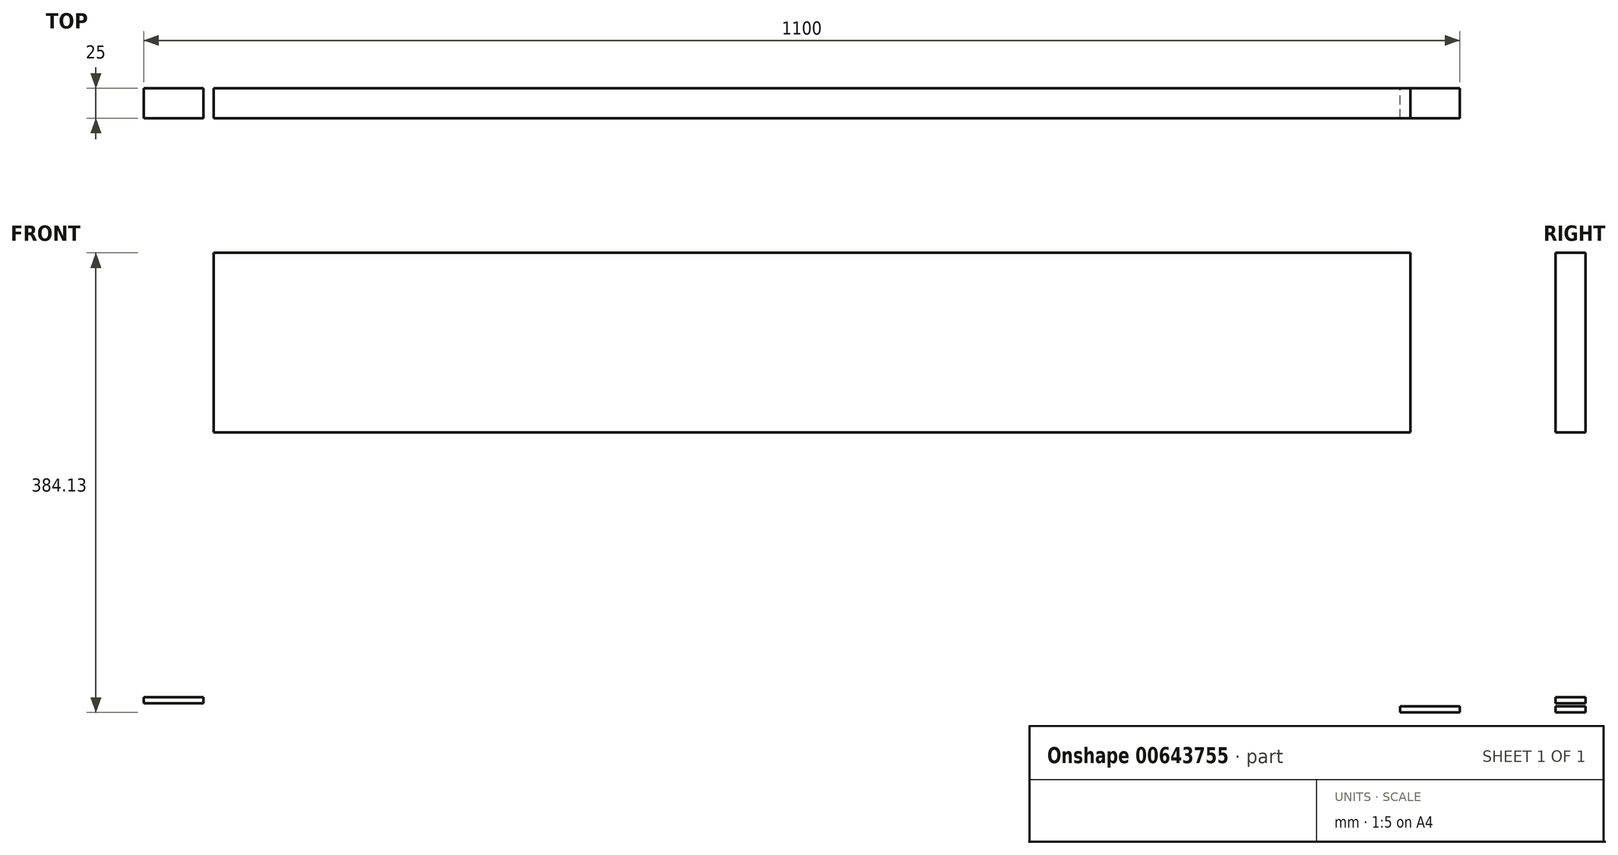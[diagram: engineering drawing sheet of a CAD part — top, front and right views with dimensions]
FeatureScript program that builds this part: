
annotation { "Feature Type Name" : "Feature", "Feature Type Description" : "" }
export const myFeature = defineFeature(function(context is Context, id is Id, definition is map)
    precondition{}
    {
        {
            var Q0;
            Q0=qCreatedBy(makeId("Front.planeOp"),FACE);
            var sketch = newSketch(context, id + "F0", { "sketchPlane" : qUnion([Q0])});
            skLineSegment(sketch, "E0.bottom", {"start": v(-524.12, -83.88) * mm, "end": v(-574.12, -83.88) * mm});
            skLineSegment(sketch, "E0.top", {"start": v(-524.12, -88.88) * mm, "end": v(-574.12, -88.88) * mm});
            skLineSegment(sketch, "E0.left", {"start": v(-524.12, -83.88) * mm, "end": v(-524.12, -88.88) * mm});
            skLineSegment(sketch, "E0.right", {"start": v(-574.12, -83.88) * mm, "end": v(-574.12, -88.88) * mm});
            skLineSegment(sketch, "E1.bottom", {"start": v(525.88, -91.45) * mm, "end": v(475.88, -91.45) * mm});
            skLineSegment(sketch, "E1.top", {"start": v(525.88, -96.45) * mm, "end": v(475.88, -96.45) * mm});
            skLineSegment(sketch, "E1.left", {"start": v(525.88, -91.45) * mm, "end": v(525.88, -96.45) * mm});
            skLineSegment(sketch, "E1.right", {"start": v(475.88, -91.45) * mm, "end": v(475.88, -96.45) * mm});
            skLineSegment(sketch, "E2.bottom", {"start": v(-308.87, 130.07) * mm, "end": v(-358.87, 130.07) * mm});
            skLineSegment(sketch, "E2.left", {"start": v(-308.87, 130.07) * mm, "end": v(-308.87, 125.07) * mm});
            skLineSegment(sketch, "E2.right", {"start": v(-358.87, 130.07) * mm, "end": v(-358.87, 125.07) * mm});
            skSolve(sketch);
        }
        {
            var Q0;
            Q0=makeQuery(id+"F0.imprint","IMPRINT",FACE,{"disambiguationData":[TD([[makeQuery(id+"F0.imprint","IMPRINT",EDGE,{"derivedFrom":sQuery(id+"F0.wireOp",EDGE,"E0.bottom")}),1.0]])]});
            var Q1;
            Q1=makeQuery(id+"F0.imprint","IMPRINT",FACE,{"disambiguationData":[TD([[makeQuery(id+"F0.imprint","IMPRINT",EDGE,{"derivedFrom":sQuery(id+"F0.wireOp",EDGE,"E1.bottom")}),1.0]])]});
            var Q2;
            Q2=makeQuery(id+"F0.imprint","IMPRINT",FACE,{"disambiguationData":[TD([[makeQuery(id+"F0.imprint","IMPRINT",EDGE,{"derivedFrom":sQuery(id+"F0.wireOp",EDGE,"E2.bottom")}),1.0]])]});
            extrude(context, id + "F1", {"entities" : qUnion([Q0, Q1, Q2]), "depth" : 25 * mm, "offsetDistance" : 25 * mm});
        }
        {
            var Q0;
            Q0=qCreatedBy(makeId("Front.planeOp"),FACE);
            var sketch = newSketch(context, id + "F2", { "sketchPlane" : qUnion([Q0])});
            skLineSegment(sketch, "E3.bottom", {"start": v(-515.6, 137.68) * mm, "end": v(484.4, 137.68) * mm});
            skLineSegment(sketch, "E3.top", {"start": v(-515.6, 287.68) * mm, "end": v(484.4, 287.68) * mm});
            skLineSegment(sketch, "E3.left", {"start": v(-515.6, 137.68) * mm, "end": v(-515.6, 287.68) * mm});
            skLineSegment(sketch, "E3.right", {"start": v(484.4, 137.68) * mm, "end": v(484.4, 287.68) * mm});
            skSolve(sketch);
        }
        {
            var Q0;
            Q0 = qSketchRegion(id + "F2", true);
            extrude(context, id + "F3", {"entities" : qUnion([Q0]), "depth" : 25 * mm, "offsetDistance" : 25 * mm});
        }
    });
